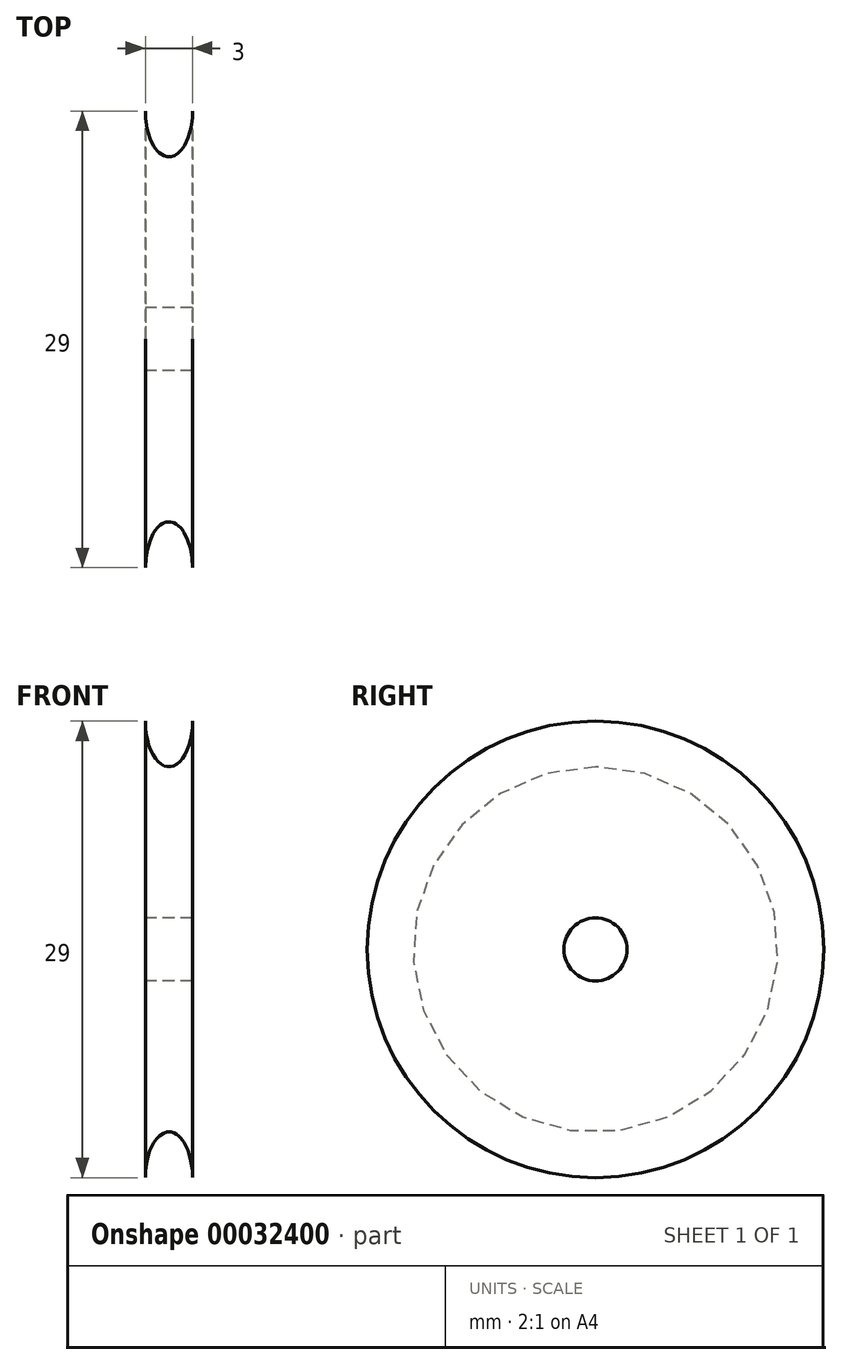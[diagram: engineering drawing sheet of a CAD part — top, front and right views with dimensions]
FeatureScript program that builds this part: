
annotation { "Feature Type Name" : "Feature", "Feature Type Description" : "" }
export const myFeature = defineFeature(function(context is Context, id is Id, definition is map)
    precondition{}
    {
        {
            var Q0;
            Q0=qCreatedBy(makeId("Front.planeOp"),FACE);
            var sketch = newSketch(context, id + "F0", { "sketchPlane" : qUnion([Q0])});
            skLineSegment(sketch, "E0", {"start": v(-1.5, 14.5) * mm, "end": v(-1.5, 0) * mm});
            skLineSegment(sketch, "E1", {"start": v(-1.5, 0) * mm, "end": v(1.5, 0) * mm});
            skLineSegment(sketch, "E2", {"start": v(1.5, 0) * mm, "end": v(1.5, 14.5) * mm});
            skEllipticalArc(sketch, "E3", {});
            const initialGuessF0  = {"E3": [0, 0.0145, -1, 0, 0.0015, 0.0029027028814772944, 6.283185307179586, 3.141592653589793]};
            skSetInitialGuess(sketch, initialGuessF0);
            skSolve(sketch);
        }
        {
            var Q0;
            Q0=makeQuery(id+"F0.imprint","IMPRINT",FACE,{"disambiguationData":[TD([[makeQuery(id+"F0.imprint","IMPRINT",EDGE,{"derivedFrom":sQuery(id+"F0.wireOp",EDGE,"E0")}),1.0]])]});
            var Q1;
            Q1=sQuery(id+"F0.wireOp",EDGE,"E1");
            revolve(context, id + "F1", {"entities" : qUnion([Q0]), "axis" : qUnion([Q1]), "revolveType" : RevolveType.FULL});
        }
        {
            var Q0;
            Q0=makeQuery(id+"F1.opRevolve","SWEPT_FACE",FACE,{"disambiguationData":[OSD([sQuery(id+"F0.wireOp",EDGE,"E0")])]});
            var sketch = newSketch(context, id + "F2", { "sketchPlane" : qUnion([Q0])});
            skCircle(sketch, "E4", {"center": v(0, 0) * mm, "radius": 2 * mm});
            skSolve(sketch);
        }
        {
            var Q0;
            Q0=makeQuery(id+"F2.imprint","IMPRINT",FACE,{"disambiguationData":[TD([[makeQuery(id+"F2.imprint","IMPRINT",EDGE,{"derivedFrom":sQuery(id+"F2.wireOp",EDGE,"E4")}),1.0]])]});
            extrude(context, id + "F3", {"entities" : qUnion([Q0]), "operationType" : NewBodyOperationType.REMOVE, "oppositeDirection" : true, "depth" : 25 * mm});
        }
    });
